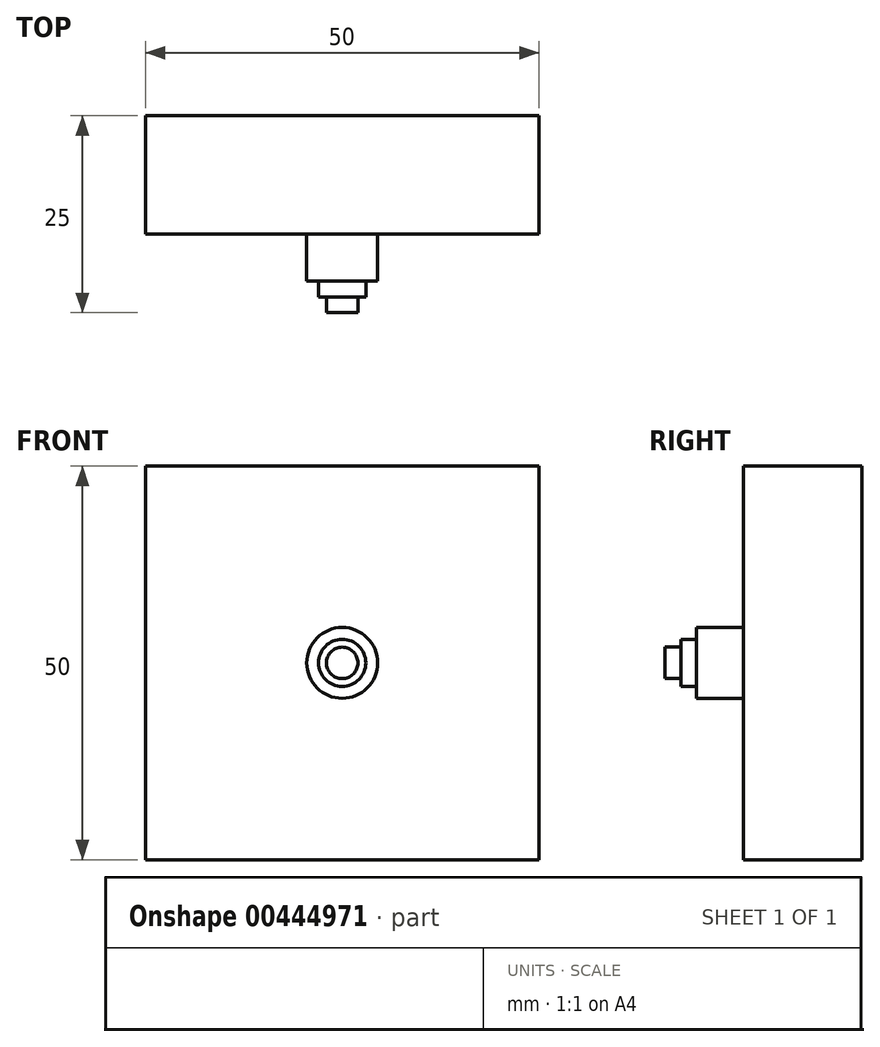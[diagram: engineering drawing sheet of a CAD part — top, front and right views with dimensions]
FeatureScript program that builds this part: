
annotation { "Feature Type Name" : "Feature", "Feature Type Description" : "" }
export const myFeature = defineFeature(function(context is Context, id is Id, definition is map)
    precondition{}
    {
        {
            var Q0;
            Q0=qCreatedBy(makeId("Front.planeOp"),FACE);
            var sketch = newSketch(context, id + "F0", { "sketchPlane" : qUnion([Q0])});
            skLineSegment(sketch, "E0.bottom", {"start": v(0, 0) * mm, "end": v(50, 0) * mm});
            skLineSegment(sketch, "E0.top", {"start": v(0, 50) * mm, "end": v(50, 50) * mm});
            skLineSegment(sketch, "E0.left", {"start": v(0, 0) * mm, "end": v(0, 50) * mm});
            skLineSegment(sketch, "E0.right", {"start": v(50, 0) * mm, "end": v(50, 50) * mm});
            skSolve(sketch);
        }
        {
            var Q0;
            Q0 = qSketchRegion(id + "F0", true);
            extrude(context, id + "F1", {"entities" : qUnion([Q0]), "depth" : 15 * mm});
        }
        {
            var Q0;
            Q0=makeQuery(id+"F1.opExtrude","CAP_FACE",FACE,{"disambiguationData":[OSD([sQuery(id+"F0.wireOp",EDGE,"E0.bottom"),sQuery(id+"F0.wireOp",EDGE,"E0.top"),sQuery(id+"F0.wireOp",EDGE,"E0.left"),sQuery(id+"F0.wireOp",EDGE,"E0.right")])],"isStart":false});
            var sketch = newSketch(context, id + "F2", { "sketchPlane" : qUnion([Q0])});
            skCircle(sketch, "E1", {"center": v(25, 25) * mm, "radius": 4.5 * mm});
            skPoint(sketch, "E1.centerSnap0", {"position": v(25, 0) * mm});
            skPoint(sketch, "E1.centerSnap1", {"position": v(0, 25) * mm});
            skSolve(sketch);
        }
        {
            var Q0;
            Q0 = qSketchRegion(id + "F2", true);
            extrude(context, id + "F3", {"entities" : qUnion([Q0]), "operationType" : NewBodyOperationType.ADD, "depth" : 10 * mm});
        }
        {
            var Q0;
            Q0=makeQuery(id+"F3.opExtrude","CAP_FACE",FACE,{"disambiguationData":[OSD([sQuery(id+"F2.wireOp",EDGE,"E1")])],"isStart":false});
            var sketch = newSketch(context, id + "F4", { "sketchPlane" : qUnion([Q0])});
            skCircle(sketch, "E2", {"center": v(25, 25) * mm, "radius": 3 * mm});
            skSolve(sketch);
        }
        {
            var Q0;
            Q0=makeQuery(id+"F4.imprint","IMPRINT",FACE,{"disambiguationData":[TD([[makeQuery(id+"F4.imprint","IMPRINT",EDGE,{"derivedFrom":sQuery(id+"F4.wireOp",EDGE,"E2")}),-1.0]])]});
            extrude(context, id + "F5", {"entities" : qUnion([Q0]), "operationType" : NewBodyOperationType.REMOVE, "oppositeDirection" : true, "depth" : 4 * mm});
        }
        {
            var Q0;
            Q0=makeQuery(id+"F3.opExtrude","CAP_FACE",FACE,{"disambiguationData":[OSD([sQuery(id+"F2.wireOp",EDGE,"E1")])],"isStart":false});
            var sketch = newSketch(context, id + "F6", { "sketchPlane" : qUnion([Q0])});
            skCircle(sketch, "E3", {"center": v(25, 25) * mm, "radius": 2 * mm});
            skSolve(sketch);
        }
        {
            var Q0;
            Q0=makeQuery(id+"F6.imprint","IMPRINT",FACE,{"disambiguationData":[TD([[makeQuery(id+"F6.imprint","IMPRINT",EDGE,{"derivedFrom":sQuery(id+"F6.wireOp",EDGE,"E3")}),-1.0]])]});
            extrude(context, id + "F7", {"entities" : qUnion([Q0]), "operationType" : NewBodyOperationType.REMOVE, "oppositeDirection" : true, "depth" : 2 * mm});
        }
    });
